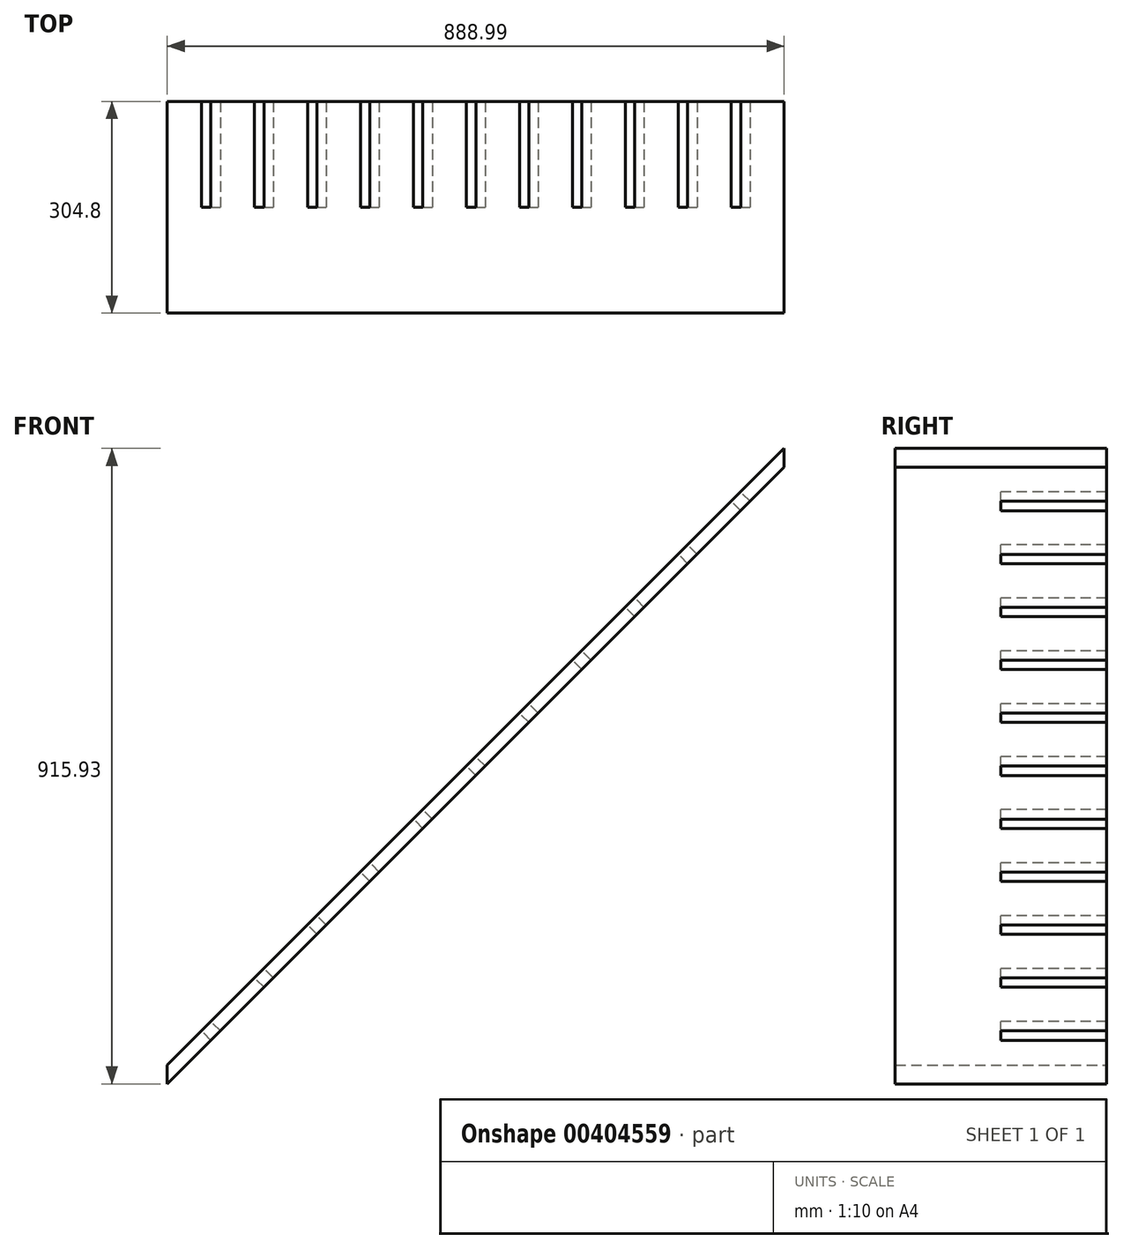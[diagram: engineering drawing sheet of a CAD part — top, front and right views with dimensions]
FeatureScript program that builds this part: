
annotation { "Feature Type Name" : "Feature", "Feature Type Description" : "" }
export const myFeature = defineFeature(function(context is Context, id is Id, definition is map)
    precondition{}
    {
        {
            var Q0;
            Q0=qCreatedBy(makeId("Front.planeOp"),FACE);
            var sketch = newSketch(context, id + "F0", { "sketchPlane" : qUnion([Q0])});
            skLineSegment(sketch, "E0.left", {"start": v(-421.52, 0) * mm, "end": v(-421.52, 26.94) * mm});
            skLineSegment(sketch, "E0.right", {"start": v(467.47, 889) * mm, "end": v(467.47, 915.93) * mm});
            skPoint(sketch, "E0.middle", {"position": v(22.97, 488.94) * mm});
            skLineSegment(sketch, "E1", {"start": v(-421.52, 0) * mm, "end": v(467.47, 889) * mm});
            skLineSegment(sketch, "E2", {"start": v(-421.52, 26.94) * mm, "end": v(467.47, 915.93) * mm});
            skSolve(sketch);
        }
        {
            var Q0;
            Q0 = qSketchRegion(id + "F0", true);
            extrude(context, id + "F1", {"entities" : qUnion([Q0]), "endBound" : BoundingType.SYMMETRIC, "depth" : 304.8 * mm});
        }
        {
            var Q0;
            Q0=makeQuery(id+"F1.opExtrude","SWEPT_FACE",FACE,{"disambiguationData":[OSD([sQuery(id+"F0.wireOp",EDGE,"E2")])]});
            var sketch = newSketch(context, id + "F2", { "sketchPlane" : qUnion([Q0])});
            skLineSegment(sketch, "E3.bottom", {"start": v(-152.4, -209.16) * mm, "end": v(0, -209.16) * mm});
            skLineSegment(sketch, "E3.top", {"start": v(-152.4, -190.11) * mm, "end": v(0, -190.11) * mm});
            skLineSegment(sketch, "E3.left", {"start": v(-152.4, -209.16) * mm, "end": v(-152.4, -190.11) * mm});
            skLineSegment(sketch, "E3.right", {"start": v(0, -209.16) * mm, "end": v(0, -190.11) * mm});
            skLineSegment(sketch, "E4.bottom", {"start": v(-152.4, -101.21) * mm, "end": v(0, -101.21) * mm});
            skLineSegment(sketch, "E4.top", {"start": v(-152.4, -82.16) * mm, "end": v(0, -82.16) * mm});
            skLineSegment(sketch, "E4.left", {"start": v(-152.4, -101.21) * mm, "end": v(-152.4, -82.16) * mm});
            skLineSegment(sketch, "E4.right", {"start": v(0, -101.21) * mm, "end": v(0, -82.16) * mm});
            skLineSegment(sketch, "E5.bottom", {"start": v(-152.4, 6.74) * mm, "end": v(0, 6.74) * mm});
            skLineSegment(sketch, "E5.top", {"start": v(-152.4, 25.79) * mm, "end": v(0, 25.79) * mm});
            skLineSegment(sketch, "E5.left", {"start": v(-152.4, 6.74) * mm, "end": v(-152.4, 25.79) * mm});
            skLineSegment(sketch, "E5.right", {"start": v(0, 6.74) * mm, "end": v(0, 25.79) * mm});
            skLineSegment(sketch, "E6.bottom", {"start": v(-152.4, 114.69) * mm, "end": v(0, 114.69) * mm});
            skLineSegment(sketch, "E6.top", {"start": v(-152.4, 133.74) * mm, "end": v(0, 133.74) * mm});
            skLineSegment(sketch, "E6.left", {"start": v(-152.4, 114.69) * mm, "end": v(-152.4, 133.74) * mm});
            skLineSegment(sketch, "E6.right", {"start": v(0, 114.69) * mm, "end": v(0, 133.74) * mm});
            skLineSegment(sketch, "E7.bottom", {"start": v(-152.4, 222.64) * mm, "end": v(0, 222.64) * mm});
            skLineSegment(sketch, "E7.top", {"start": v(-152.4, 241.69) * mm, "end": v(0, 241.69) * mm});
            skLineSegment(sketch, "E7.left", {"start": v(-152.4, 222.64) * mm, "end": v(-152.4, 241.69) * mm});
            skLineSegment(sketch, "E7.right", {"start": v(0, 222.64) * mm, "end": v(0, 241.69) * mm});
            skLineSegment(sketch, "E8.bottom", {"start": v(-152.4, 330.59) * mm, "end": v(0, 330.59) * mm});
            skLineSegment(sketch, "E8.top", {"start": v(-152.4, 349.64) * mm, "end": v(0, 349.64) * mm});
            skLineSegment(sketch, "E8.left", {"start": v(-152.4, 330.59) * mm, "end": v(-152.4, 349.64) * mm});
            skLineSegment(sketch, "E8.right", {"start": v(0, 330.59) * mm, "end": v(0, 349.64) * mm});
            skLineSegment(sketch, "E9.bottom", {"start": v(-152.4, 438.54) * mm, "end": v(0, 438.54) * mm});
            skLineSegment(sketch, "E9.top", {"start": v(-152.4, 457.59) * mm, "end": v(0, 457.59) * mm});
            skLineSegment(sketch, "E9.left", {"start": v(-152.4, 438.54) * mm, "end": v(-152.4, 457.59) * mm});
            skLineSegment(sketch, "E9.right", {"start": v(0, 438.54) * mm, "end": v(0, 457.59) * mm});
            skLineSegment(sketch, "E10.bottom", {"start": v(-152.4, 546.49) * mm, "end": v(0, 546.49) * mm});
            skLineSegment(sketch, "E10.top", {"start": v(-152.4, 565.54) * mm, "end": v(0, 565.54) * mm});
            skLineSegment(sketch, "E10.left", {"start": v(-152.4, 546.49) * mm, "end": v(-152.4, 565.54) * mm});
            skLineSegment(sketch, "E10.right", {"start": v(0, 546.49) * mm, "end": v(0, 565.54) * mm});
            skLineSegment(sketch, "E11.bottom", {"start": v(-152.4, 654.44) * mm, "end": v(0, 654.44) * mm});
            skLineSegment(sketch, "E11.top", {"start": v(-152.4, 673.49) * mm, "end": v(0, 673.49) * mm});
            skLineSegment(sketch, "E11.left", {"start": v(-152.4, 654.44) * mm, "end": v(-152.4, 673.49) * mm});
            skLineSegment(sketch, "E11.right", {"start": v(0, 654.44) * mm, "end": v(0, 673.49) * mm});
            skLineSegment(sketch, "E12.bottom", {"start": v(-152.4, 762.39) * mm, "end": v(0, 762.39) * mm});
            skLineSegment(sketch, "E12.top", {"start": v(-152.4, 781.44) * mm, "end": v(0, 781.44) * mm});
            skLineSegment(sketch, "E12.left", {"start": v(-152.4, 762.39) * mm, "end": v(-152.4, 781.44) * mm});
            skLineSegment(sketch, "E12.right", {"start": v(0, 762.39) * mm, "end": v(0, 781.44) * mm});
            skLineSegment(sketch, "E13.bottom", {"start": v(-152.4, 870.34) * mm, "end": v(0, 870.34) * mm});
            skLineSegment(sketch, "E13.top", {"start": v(-152.4, 889.39) * mm, "end": v(0, 889.39) * mm});
            skLineSegment(sketch, "E13.left", {"start": v(-152.4, 870.34) * mm, "end": v(-152.4, 889.39) * mm});
            skLineSegment(sketch, "E13.right", {"start": v(0, 870.34) * mm, "end": v(0, 889.39) * mm});
            skSolve(sketch);
        }
        {
            var Q0;
            Q0 = qSketchRegion(id + "F2", true);
            extrude(context, id + "F3", {"entities" : qUnion([Q0]), "operationType" : NewBodyOperationType.REMOVE, "oppositeDirection" : true, "depth" : 19.05 * mm});
        }
    });
